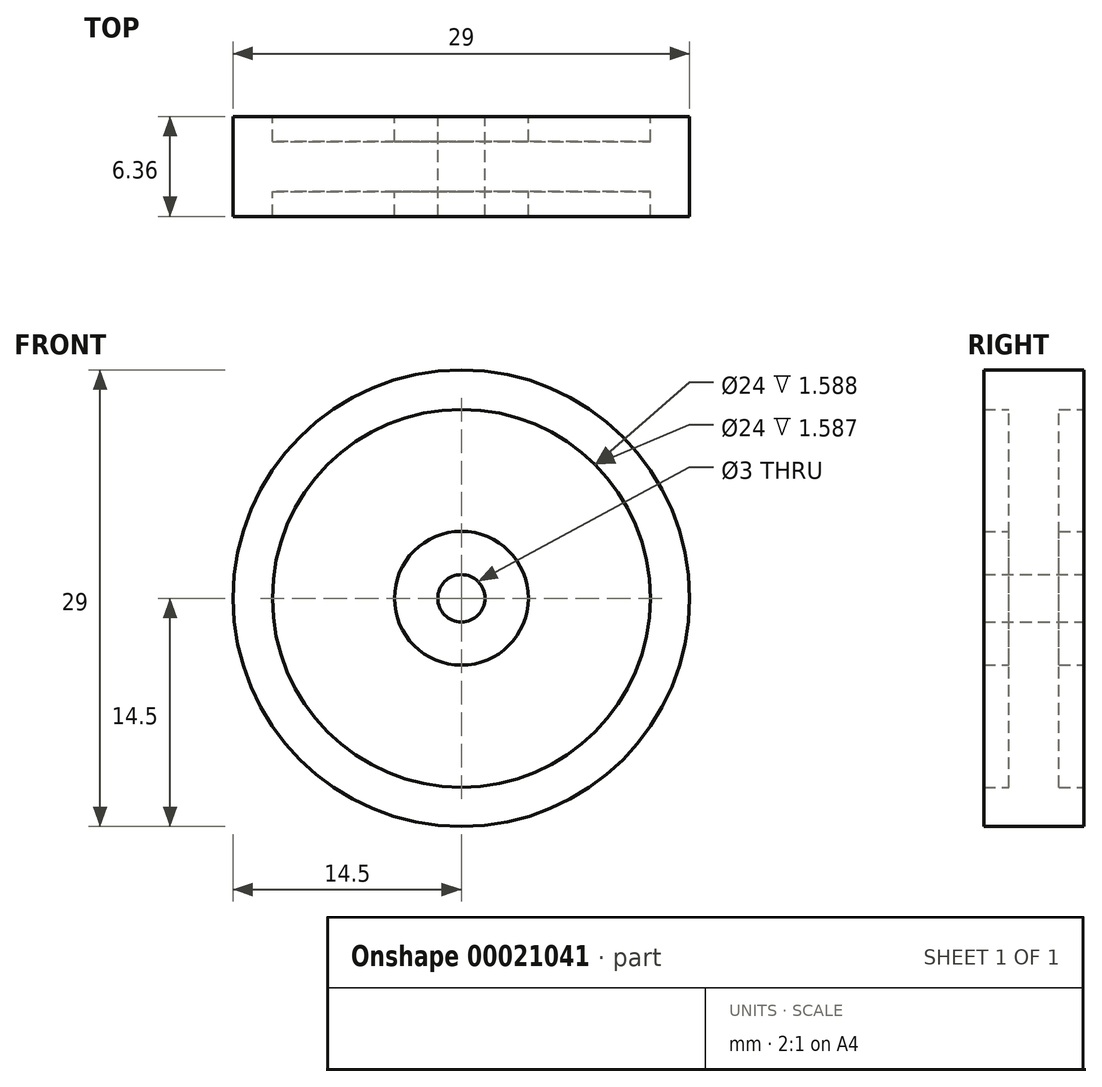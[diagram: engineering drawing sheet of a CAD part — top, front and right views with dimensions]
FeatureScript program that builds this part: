
annotation { "Feature Type Name" : "Feature", "Feature Type Description" : "" }
export const myFeature = defineFeature(function(context is Context, id is Id, definition is map)
    precondition{}
    {
        {
            var Q0;
            Q0=qCreatedBy(makeId("Front.planeOp"),FACE);
            var sketch = newSketch(context, id + "F0", { "sketchPlane" : qUnion([Q0])});
            skCircle(sketch, "E0", {"center": v(0, 0) * mm, "radius": 4.25 * mm});
            skCircle(sketch, "E1", {"center": v(0, 0) * mm, "radius": 1.5 * mm});
            skCircle(sketch, "E2", {"center": v(0, 0) * mm, "radius": 12 * mm});
            skCircle(sketch, "E3", {"center": v(0, 0) * mm, "radius": 14.5 * mm});
            skSolve(sketch);
        }
        {
            var Q0;
            Q0 = qSketchRegion(id + "F0", true);
            extrude(context, id + "F1", {"entities" : qUnion([Q0]), "endBound" : BoundingType.SYMMETRIC, "depth" : 6.35 * mm});
        }
        {
            var Q0;
            Q0=makeQuery(id+"F0.imprint","IMPRINT",FACE,{"disambiguationData":[TD([[makeQuery(id+"F0.imprint","IMPRINT",EDGE,{"derivedFrom":sQuery(id+"F0.wireOp",EDGE,"E0")}),-1.0]])]});
            extrude(context, id + "F2", {"entities" : qUnion([Q0]), "operationType" : NewBodyOperationType.ADD, "endBound" : BoundingType.SYMMETRIC, "depth" : 3.17 * mm});
        }
        {
            var Q0;
            Q0=makeQuery(id+"F0.imprint","IMPRINT",FACE,{"disambiguationData":[TD([[makeQuery(id+"F0.imprint","IMPRINT",EDGE,{"derivedFrom":sQuery(id+"F0.wireOp",EDGE,"E0")}),1.0]])]});
            extrude(context, id + "F3", {"entities" : qUnion([Q0]), "operationType" : NewBodyOperationType.ADD, "endBound" : BoundingType.SYMMETRIC, "depth" : 6.35 * mm});
        }
    });
